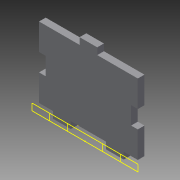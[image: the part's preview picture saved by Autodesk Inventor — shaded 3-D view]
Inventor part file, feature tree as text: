
AUTODESK INVENTOR PART (.ipt)
format: ipt  version: 2015 SP1 (Build 190203100, 203)  size: 116,224 bytes
history: native  units: in
note: dims shown in document units (in); Inventor stores cm internally (conversion verified against a paired STEP export)
features: reference x7, sketch x3, extrude x2, plane x1
ambient origin geometry x8: Origin, YZ Plane, XZ Plane, XY Plane, X Axis, Y Axis, Z Axis, Center Point
bodies: Solid1 (feature_tree)
feature tree (13):
  sketch  "Sketch1"  dims[d0=2.0in d2=0.5in]
  plane  "Work Plane1"
  extrude  "Extrusion1"  Depth=0.5in
  extrude  "Extrusion2"  Depth=0.19in TaperAngle=0.0deg
  reference  "Reference1"
  reference  "Reference2"
  reference  "Reference3"
  sketch  "Sketch2"  dims[d5=0.19in d6=0.19in d7=0.0in]
  reference  "Reference4"
  reference  "Reference5"
  reference  "Reference6"
  reference  "Reference7"
  sketch  "Sketch3"  dims[d8=0.5in d9=0.19in d10=1.15in d11=0.19in d12=0.0in d13=0.75in d14=0.75in d15=0.5in]
